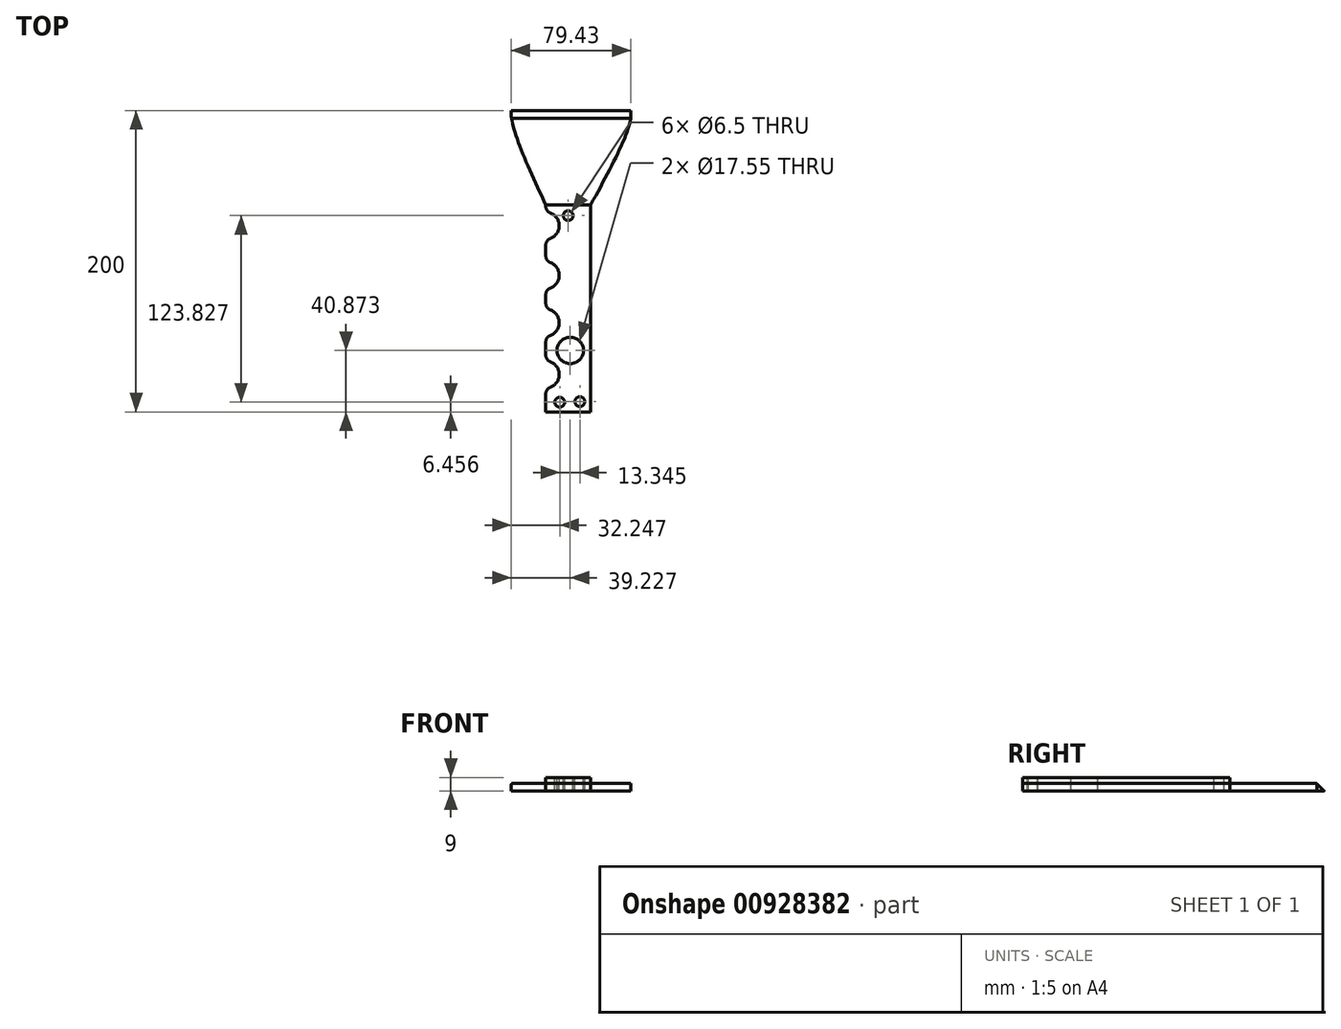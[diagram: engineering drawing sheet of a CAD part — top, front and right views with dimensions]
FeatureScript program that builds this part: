
annotation { "Feature Type Name" : "Feature", "Feature Type Description" : "" }
export const myFeature = defineFeature(function(context is Context, id is Id, definition is map)
    precondition{}
    {
        {
            var Q0;
            Q0=qCreatedBy(makeId("Top.planeOp"),FACE);
            var sketch = newSketch(context, id + "F0", { "sketchPlane" : qUnion([Q0])});
            skLineSegment(sketch, "E0.bottom", {"start": v(0, 0) * mm, "end": v(-80, 0) * mm});
            skLineSegment(sketch, "E0.top", {"start": v(0, 200) * mm, "end": v(-80, 200) * mm});
            skLineSegment(sketch, "E0.left", {"start": v(0, 0) * mm, "end": v(0, 200) * mm});
            skLineSegment(sketch, "E0.right", {"start": v(-80, 0) * mm, "end": v(-80, 200) * mm});
            skSolve(sketch);
        }
        {
            var Q0;
            Q0=makeQuery(id+"F0.imprint","IMPRINT",FACE,{"disambiguationData":[TD([[makeQuery(id+"F0.imprint","IMPRINT",EDGE,{"derivedFrom":sQuery(id+"F0.wireOp",EDGE,"E0.bottom")}),-1.0]])]});
            var sketch = newSketch(context, id + "F1", { "sketchPlane" : qUnion([Q0])});
            skLineSegment(sketch, "E1", {"start": v(-80.07, 137.47) * mm, "end": v(0, 137.47) * mm});
            skLineSegment(sketch, "E2", {"start": v(-56.5, 137.47) * mm, "end": v(-56.5, 0) * mm});
            skLineSegment(sketch, "E3", {"start": v(-26.58, 137.47) * mm, "end": v(-26.58, 0) * mm});
            skFitSpline(sketch, "E4", {"points": [v(-56.5, 137.47) * mm, v(-79.33, 199.94) * mm, v(-74.46, 207.04) * mm], "startDerivative": vector(-49.2, 106.3) * mm, "endDerivative": vector(24.91, 19.17) * mm});
            skFitSpline(sketch, "E5", {"points": [v(-26.58, 137.47) * mm, v(0, 199.94) * mm, v(-6.76, 205.92) * mm], "startDerivative": vector(58.84, 108.28) * mm, "endDerivative": vector(-33.52, 14) * mm});
            skSolve(sketch);
        }
        {
            var Q0;
            {var subQ0=sQuery(id+"F1.wireOp",EDGE,"E5");var subQ1=makeQuery(id+"F0.imprint","IMPRINT",EDGE,{"derivedFrom":sQuery(id+"F0.wireOp",EDGE,"E0.top")});var subQ2=makeQuery(id+"F1.imprint","INTERSECT",VERTEX,{"derivedFrom":[subQ1,subQ0]});Q0=makeQuery(id+"F1.imprint","IMPRINT",FACE,{"disambiguationData":[TD([[makeQuery(id+"F1.imprint","IMPRINT",EDGE,{"disambiguationData":[TD([[subQ2,1.0]])],"derivedFrom":subQ0}),1.0]])]});}
            var Q1;
            {var subQ0=sQuery(id+"F1.wireOp",EDGE,"E2");Q1=makeQuery(id+"F1.imprint","IMPRINT",FACE,{"disambiguationData":[TD([[makeQuery(id+"F1.imprint","IMPRINT",EDGE,{"derivedFrom":subQ0}),1.0]])]});}
            extrude(context, id + "F2", {"entities" : qUnion([Q0, Q1]), "depth" : 5 * mm, "offsetDistance" : 25 * mm});
        }
        {
            var Q0;
            Q0=makeQuery(id+"F2.opExtrude","CAP_FACE",FACE,{"disambiguationData":[OSD([sQuery(id+"F0.wireOp",EDGE,"E0.bottom"),sQuery(id+"F0.wireOp",EDGE,"E0.top"),sQuery(id+"F0.wireOp",EDGE,"E0.left"),sQuery(id+"F1.wireOp",EDGE,"E2"),sQuery(id+"F1.wireOp",EDGE,"E3"),sQuery(id+"F1.wireOp",EDGE,"E4"),sQuery(id+"F1.wireOp",EDGE,"E5")])],"isStart":false});
            var sketch = newSketch(context, id + "F3", { "sketchPlane" : qUnion([Q0])});
            skCircle(sketch, "E6", {"center": v(-56.5, 123.63) * mm, "radius": 9 * mm});
            skCircle(sketch, "E7", {"center": v(-56.5, 90.71) * mm, "radius": 9 * mm});
            skCircle(sketch, "E8", {"center": v(-56.5, 59.3) * mm, "radius": 9 * mm});
            skCircle(sketch, "E9", {"center": v(-56.5, 24.88) * mm, "radius": 9 * mm});
            skSolve(sketch);
        }
        {
            var Q0;
            {var subQ0=sQuery(id+"F3.wireOp",EDGE,"E6");var subQ1=makeQuery(id+"F2.opExtrude","CAP_EDGE",EDGE,{"disambiguationData":[OSD([sQuery(id+"F1.wireOp",EDGE,"E2")])],"isStart":false});var subQ2=makeQuery(id+"F3.imprint","INTERSECT",VERTEX,{"disambiguationData":[OD(0.0)],"derivedFrom":[subQ1,subQ0]});Q0=makeQuery(id+"F3.imprint","IMPRINT",FACE,{"disambiguationData":[TD([[makeQuery(id+"F3.imprint","IMPRINT",EDGE,{"disambiguationData":[TD([[subQ2,-1.0]])],"derivedFrom":subQ0}),1.0]])]});}
            var Q1;
            {var subQ0=sQuery(id+"F3.wireOp",EDGE,"E6");var subQ1=makeQuery(id+"F2.opExtrude","CAP_EDGE",EDGE,{"disambiguationData":[OSD([sQuery(id+"F1.wireOp",EDGE,"E2")])],"isStart":false});var subQ2=makeQuery(id+"F3.imprint","INTERSECT",VERTEX,{"disambiguationData":[OD(0.0)],"derivedFrom":[subQ1,subQ0]});Q1=makeQuery(id+"F3.imprint","IMPRINT",FACE,{"disambiguationData":[TD([[makeQuery(id+"F3.imprint","IMPRINT",EDGE,{"disambiguationData":[TD([[subQ2,1.0]])],"derivedFrom":subQ0}),1.0]])]});}
            var Q2;
            {var subQ0=sQuery(id+"F3.wireOp",EDGE,"E7");var subQ1=makeQuery(id+"F2.opExtrude","CAP_EDGE",EDGE,{"disambiguationData":[OSD([sQuery(id+"F1.wireOp",EDGE,"E2")])],"isStart":false});var subQ2=makeQuery(id+"F3.imprint","INTERSECT",VERTEX,{"disambiguationData":[OD(0.0)],"derivedFrom":[subQ1,subQ0]});Q2=makeQuery(id+"F3.imprint","IMPRINT",FACE,{"disambiguationData":[TD([[makeQuery(id+"F3.imprint","IMPRINT",EDGE,{"disambiguationData":[TD([[subQ2,1.0]])],"derivedFrom":subQ0}),1.0]])]});}
            var Q3;
            {var subQ0=sQuery(id+"F3.wireOp",EDGE,"E7");var subQ1=makeQuery(id+"F2.opExtrude","CAP_EDGE",EDGE,{"disambiguationData":[OSD([sQuery(id+"F1.wireOp",EDGE,"E2")])],"isStart":false});var subQ2=makeQuery(id+"F3.imprint","INTERSECT",VERTEX,{"disambiguationData":[OD(0.0)],"derivedFrom":[subQ1,subQ0]});Q3=makeQuery(id+"F3.imprint","IMPRINT",FACE,{"disambiguationData":[TD([[makeQuery(id+"F3.imprint","IMPRINT",EDGE,{"disambiguationData":[TD([[subQ2,-1.0]])],"derivedFrom":subQ0}),1.0]])]});}
            var Q4;
            {var subQ0=sQuery(id+"F3.wireOp",EDGE,"E8");var subQ1=makeQuery(id+"F2.opExtrude","CAP_EDGE",EDGE,{"disambiguationData":[OSD([sQuery(id+"F1.wireOp",EDGE,"E2")])],"isStart":false});var subQ2=makeQuery(id+"F3.imprint","INTERSECT",VERTEX,{"disambiguationData":[OD(0.0)],"derivedFrom":[subQ1,subQ0]});Q4=makeQuery(id+"F3.imprint","IMPRINT",FACE,{"disambiguationData":[TD([[makeQuery(id+"F3.imprint","IMPRINT",EDGE,{"disambiguationData":[TD([[subQ2,1.0]])],"derivedFrom":subQ0}),1.0]])]});}
            var Q5;
            {var subQ0=sQuery(id+"F3.wireOp",EDGE,"E8");var subQ1=makeQuery(id+"F2.opExtrude","CAP_EDGE",EDGE,{"disambiguationData":[OSD([sQuery(id+"F1.wireOp",EDGE,"E2")])],"isStart":false});var subQ2=makeQuery(id+"F3.imprint","INTERSECT",VERTEX,{"disambiguationData":[OD(0.0)],"derivedFrom":[subQ1,subQ0]});Q5=makeQuery(id+"F3.imprint","IMPRINT",FACE,{"disambiguationData":[TD([[makeQuery(id+"F3.imprint","IMPRINT",EDGE,{"disambiguationData":[TD([[subQ2,-1.0]])],"derivedFrom":subQ0}),1.0]])]});}
            var Q6;
            {var subQ0=sQuery(id+"F3.wireOp",EDGE,"E9");var subQ1=makeQuery(id+"F2.opExtrude","CAP_EDGE",EDGE,{"disambiguationData":[OSD([sQuery(id+"F1.wireOp",EDGE,"E2")])],"isStart":false});var subQ2=makeQuery(id+"F3.imprint","INTERSECT",VERTEX,{"disambiguationData":[OD(0.0)],"derivedFrom":[subQ1,subQ0]});Q6=makeQuery(id+"F3.imprint","IMPRINT",FACE,{"disambiguationData":[TD([[makeQuery(id+"F3.imprint","IMPRINT",EDGE,{"disambiguationData":[TD([[subQ2,-1.0]])],"derivedFrom":subQ0}),1.0]])]});}
            var Q7;
            {var subQ0=sQuery(id+"F3.wireOp",EDGE,"E9");var subQ1=makeQuery(id+"F2.opExtrude","CAP_EDGE",EDGE,{"disambiguationData":[OSD([sQuery(id+"F1.wireOp",EDGE,"E2")])],"isStart":false});var subQ2=makeQuery(id+"F3.imprint","INTERSECT",VERTEX,{"disambiguationData":[OD(0.0)],"derivedFrom":[subQ1,subQ0]});Q7=makeQuery(id+"F3.imprint","IMPRINT",FACE,{"disambiguationData":[TD([[makeQuery(id+"F3.imprint","IMPRINT",EDGE,{"disambiguationData":[TD([[subQ2,1.0]])],"derivedFrom":subQ0}),1.0]])]});}
            extrude(context, id + "F4", {"entities" : qUnion([Q0, Q1, Q2, Q3, Q4, Q5, Q6, Q7]), "operationType" : NewBodyOperationType.REMOVE, "oppositeDirection" : true, "depth" : 25 * mm, "offsetDistance" : 25 * mm});
        }
        {
            var Q0;
            Q0=makeQuery(id+"F4.boolean.opBoolean","INTERSECT",EDGE,{"disambiguationData":[OD(0.0)],"derivedFrom":[makeQuery(id+"F2.opExtrude","SWEPT_FACE",FACE,{"disambiguationData":[OSD([sQuery(id+"F1.wireOp",EDGE,"E2")])]}),makeQuery(id+"F4.opExtrude","SWEPT_FACE",FACE,{"disambiguationData":[OSD([sQuery(id+"F3.wireOp",EDGE,"E6")])]})]});
            var Q1;
            Q1=makeQuery(id+"F4.boolean.opBoolean","INTERSECT",EDGE,{"disambiguationData":[OD(0.0)],"derivedFrom":[makeQuery(id+"F2.opExtrude","SWEPT_FACE",FACE,{"disambiguationData":[OSD([sQuery(id+"F1.wireOp",EDGE,"E2")])]}),makeQuery(id+"F4.opExtrude","SWEPT_FACE",FACE,{"disambiguationData":[OSD([sQuery(id+"F3.wireOp",EDGE,"E8")])]})]});
            var Q2;
            Q2=makeQuery(id+"F4.boolean.opBoolean","INTERSECT",EDGE,{"disambiguationData":[OD(1.0)],"derivedFrom":[makeQuery(id+"F2.opExtrude","SWEPT_FACE",FACE,{"disambiguationData":[OSD([sQuery(id+"F1.wireOp",EDGE,"E2")])]}),makeQuery(id+"F4.opExtrude","SWEPT_FACE",FACE,{"disambiguationData":[OSD([sQuery(id+"F3.wireOp",EDGE,"E9")])]})]});
            var Q3;
            Q3=makeQuery(id+"F4.boolean.opBoolean","INTERSECT",EDGE,{"disambiguationData":[OD(1.0)],"derivedFrom":[makeQuery(id+"F2.opExtrude","SWEPT_FACE",FACE,{"disambiguationData":[OSD([sQuery(id+"F1.wireOp",EDGE,"E2")])]}),makeQuery(id+"F4.opExtrude","SWEPT_FACE",FACE,{"disambiguationData":[OSD([sQuery(id+"F3.wireOp",EDGE,"E7")])]})]});
            var Q4;
            Q4=makeQuery(id+"F4.boolean.opBoolean","INTERSECT",EDGE,{"disambiguationData":[OD(0.0)],"derivedFrom":[makeQuery(id+"F2.opExtrude","SWEPT_FACE",FACE,{"disambiguationData":[OSD([sQuery(id+"F1.wireOp",EDGE,"E2")])]}),makeQuery(id+"F4.opExtrude","SWEPT_FACE",FACE,{"disambiguationData":[OSD([sQuery(id+"F3.wireOp",EDGE,"E9")])]})]});
            fillet(context, id + "F5", {"entities" : qUnion([Q0, Q1, Q2, Q3, Q4]), "radius" : 5 * mm, "tangentPropagation" : true, "allowEdgeOverflow" : false});
        }
        {
            var Q0;
            Q0=makeQuery(id+"F4.boolean.opBoolean","INTERSECT",EDGE,{"disambiguationData":[OD(0.0)],"derivedFrom":[makeQuery(id+"F2.opExtrude","SWEPT_FACE",FACE,{"disambiguationData":[OSD([sQuery(id+"F1.wireOp",EDGE,"E2")])]}),makeQuery(id+"F4.opExtrude","SWEPT_FACE",FACE,{"disambiguationData":[OSD([sQuery(id+"F3.wireOp",EDGE,"E7")])]})]});
            var Q1;
            Q1=makeQuery(id+"F4.boolean.opBoolean","INTERSECT",EDGE,{"disambiguationData":[OD(1.0)],"derivedFrom":[makeQuery(id+"F2.opExtrude","SWEPT_FACE",FACE,{"disambiguationData":[OSD([sQuery(id+"F1.wireOp",EDGE,"E2")])]}),makeQuery(id+"F4.opExtrude","SWEPT_FACE",FACE,{"disambiguationData":[OSD([sQuery(id+"F3.wireOp",EDGE,"E6")])]})]});
            var Q2;
            Q2=makeQuery(id+"F4.boolean.opBoolean","INTERSECT",EDGE,{"disambiguationData":[OD(1.0)],"derivedFrom":[makeQuery(id+"F2.opExtrude","SWEPT_FACE",FACE,{"disambiguationData":[OSD([sQuery(id+"F1.wireOp",EDGE,"E2")])]}),makeQuery(id+"F4.opExtrude","SWEPT_FACE",FACE,{"disambiguationData":[OSD([sQuery(id+"F3.wireOp",EDGE,"E8")])]})]});
            fillet(context, id + "F6", {"entities" : qUnion([Q0, Q1, Q2]), "radius" : 5 * mm, "tangentPropagation" : true, "allowEdgeOverflow" : false});
        }
        {
            var Q0;
            Q0=makeQuery(id+"F2.opExtrude","CAP_FACE",FACE,{"disambiguationData":[OSD([sQuery(id+"F0.wireOp",EDGE,"E0.bottom"),sQuery(id+"F0.wireOp",EDGE,"E0.top"),sQuery(id+"F0.wireOp",EDGE,"E0.left"),sQuery(id+"F1.wireOp",EDGE,"E2"),sQuery(id+"F1.wireOp",EDGE,"E3"),sQuery(id+"F1.wireOp",EDGE,"E4"),sQuery(id+"F1.wireOp",EDGE,"E5")])],"isStart":false});
            var sketch = newSketch(context, id + "F7", { "sketchPlane" : qUnion([Q0])});
            skLineSegment(sketch, "E10", {"start": v(-56.5, 137.47) * mm, "end": v(-26.58, 137.47) * mm});
            skSolve(sketch);
        }
        {
            var Q0;
            Q0=makeQuery(id+"F7.imprint","IMPRINT",FACE,{"disambiguationData":[TD([[makeQuery(id+"F7.imprint","IMPRINT",EDGE,{"derivedFrom":sQuery(id+"F7.wireOp",EDGE,"E10")}),-1.0]])]});
            extrude(context, id + "F8", {"entities" : qUnion([Q0]), "depth" : 4 * mm, "offsetDistance" : 25 * mm});
        }
        {
            var Q0;
            Q0=makeQuery(id+"F8.opExtrude","CAP_FACE",FACE,{"disambiguationData":[OSD([sQuery(id+"F0.wireOp",EDGE,"E0.bottom"),sQuery(id+"F0.wireOp",EDGE,"E0.top"),sQuery(id+"F0.wireOp",EDGE,"E0.left"),sQuery(id+"F1.wireOp",EDGE,"E2"),sQuery(id+"F1.wireOp",EDGE,"E3"),sQuery(id+"F1.wireOp",EDGE,"E4"),sQuery(id+"F1.wireOp",EDGE,"E5"),sQuery(id+"F3.wireOp",EDGE,"E6"),sQuery(id+"F3.wireOp",EDGE,"E7"),sQuery(id+"F3.wireOp",EDGE,"E8"),sQuery(id+"F3.wireOp",EDGE,"E9"),sQuery(id+"F7.wireOp",EDGE,"E10")])],"isStart":false});
            var sketch = newSketch(context, id + "F9", { "sketchPlane" : qUnion([Q0])});
            skCircle(sketch, "E11", {"center": v(-47.18, 6.46) * mm, "radius": 3.25 * mm});
            skCircle(sketch, "E12", {"center": v(-40.2, 40.87) * mm, "radius": 8.77 * mm});
            skCircle(sketch, "E13", {"center": v(-41.55, 130.28) * mm, "radius": 3.25 * mm});
            skPoint(sketch, "E13.centerSnap0", {"position": v(-41.55, 137.47) * mm});
            skCircle(sketch, "E14", {"center": v(-33.84, 6.87) * mm, "radius": 3.25 * mm});
            skSolve(sketch);
        }
        {
            var Q0;
            Q0=makeQuery(id+"F2.opExtrude","CAP_EDGE",EDGE,{"disambiguationData":[OSD([sQuery(id+"F0.wireOp",EDGE,"E0.top")])],"isStart":false});
            chamfer(context, id + "F10", {"entities" : qUnion([Q0]), "width" : 5 * mm, "tangentPropagation" : true});
        }
        {
            var Q0;
            Q0=makeQuery(id+"F9.imprint","IMPRINT",FACE,{"disambiguationData":[TD([[makeQuery(id+"F9.imprint","IMPRINT",EDGE,{"derivedFrom":sQuery(id+"F9.wireOp",EDGE,"E12")}),1.0]])]});
            var Q1;
            Q1=makeQuery(id+"F9.imprint","IMPRINT",FACE,{"disambiguationData":[TD([[makeQuery(id+"F9.imprint","IMPRINT",EDGE,{"derivedFrom":sQuery(id+"F9.wireOp",EDGE,"E11")}),1.0]])]});
            var Q2;
            Q2=makeQuery(id+"F9.imprint","IMPRINT",FACE,{"disambiguationData":[TD([[makeQuery(id+"F9.imprint","IMPRINT",EDGE,{"derivedFrom":sQuery(id+"F9.wireOp",EDGE,"E14")}),1.0]])]});
            var Q3;
            Q3=makeQuery(id+"F9.imprint","IMPRINT",FACE,{"disambiguationData":[TD([[makeQuery(id+"F9.imprint","IMPRINT",EDGE,{"derivedFrom":sQuery(id+"F9.wireOp",EDGE,"E13")}),1.0]])]});
            extrude(context, id + "F11", {"entities" : qUnion([Q0, Q1, Q2, Q3]), "operationType" : NewBodyOperationType.REMOVE, "oppositeDirection" : true, "depth" : 25 * mm, "offsetDistance" : 25 * mm});
        }
    });
